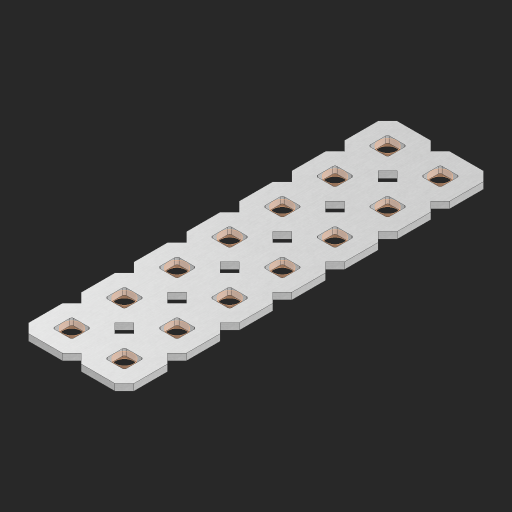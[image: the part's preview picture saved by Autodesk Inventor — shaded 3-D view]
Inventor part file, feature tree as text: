
AUTODESK INVENTOR PART (.ipt)
format: ipt  version: 2023 (Build 270158000, 158)  size: 445,440 bytes
history: native  units: in
note: dims shown in document units (in); Inventor stores cm internally (conversion verified against a paired STEP export)
features: other x15, extrude x13, sketch x2, pattern_linear x1
ambient origin geometry x8: Origin, YZ Plane, XZ Plane, XY Plane, X Axis, Y Axis, Z Axis, Center Point
bodies: Solid1 (feature_tree), Body (feature_tree)
feature tree (31):
  pattern_linear  "Rectangular Pattern1"  Spacing1=0.09in  [1 undecoded]
  sketch  "Sketch1"  dims[d1=0.5in]
  sketch  "Sketch2"  dims[d2=0.182in d3=0.09in d4=0.09in d5=0.09in d6=0.09in d7=0.09in d8=0.09in d9=0.09in d10=0.09in d11=0.02in d13=0.0in d14=0.172in d15=0.0625in d16=0.0in d19=0.5in d22=0.5in]
  other  "Srf1"
  other  "Srf126"
  other  "Srf127"
  other  "Srf128"
  other  "Srf129"
  other  "Srf130"
  other  "Srf131"
  other  "Srf268"
  other  "Srf269"
  other  "Srf270"
  other  "Srf271"
  other  "Srf272"
  other  "Srf273"
  other  "Srf274"
  other  "Circle"
  extrude  "ExtrusionSrf126"  Depth=0.09in
  extrude  "ExtrusionSrf127"  Depth=0.09in
  extrude  "ExtrusionSrf128"  Depth=0.09in
  extrude  "ExtrusionSrf129"  Depth=0.09in
  extrude  "ExtrusionSrf130"  Depth=0.09in
  extrude  "ExtrusionSrf131"  Depth=0.09in
  extrude  "ExtrusionSrf268"  Depth=0.09in
  extrude  "ExtrusionSrf269"  Depth=0.02in
  extrude  "ExtrusionSrf270"  TaperAngle=0.0deg  [1 undecoded]
  extrude  "ExtrusionSrf271"  Depth=0.5in
  extrude  "ExtrusionSrf272"  Depth=0.0625in TaperAngle=0.0deg
  extrude  "ExtrusionSrf273"  Depth=0.5in
  extrude  "ExtrusionSrf274"  Depth=0.5in
note: 2 required parameter values undecoded (feature->parameter linkage not recoverable at this tier; creation-order binding heuristic only, values carry confidence <= 0.55)
